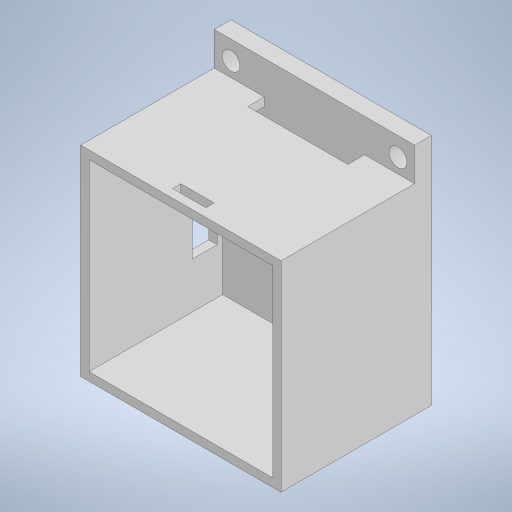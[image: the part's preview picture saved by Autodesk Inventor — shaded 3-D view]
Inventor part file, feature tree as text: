
AUTODESK INVENTOR PART (.ipt)
format: ipt  version: 2023 (Build 270158000, 158)  size: 266,240 bytes
history: native  units: in
note: dims shown in document units (in); Inventor stores cm internally (conversion verified against a paired STEP export)
features: extrude x5, sketch x5, projected_geometry x4
ambient origin geometry x8: Origin, YZ Plane, XZ Plane, XY Plane, X Axis, Y Axis, Z Axis, Center Point
bodies: Solid1 (feature_tree)
feature tree (14):
  extrude  "Extrusion1"  Depth=3.0in
  extrude  "Extrusion2"  Depth=1.5in
  extrude  "Extrusion4"  Depth=0.125in
  extrude  "Extrusion5"  Depth=0.125in
  extrude  "Extrusion6"  Depth=2.0in TaperAngle=0.0deg
  sketch  "Sketch1"  dims[d0=3.0in d1=3.0in]
  sketch  "Sketch2"  dims[d2=1.5in d3=1.5in]
  sketch  "Sketch4"  dims[d4=0.25in d5=0.0in d6=0.125in]
  projected_geometry  "Projected Loop1"
  sketch  "Sketch5"  dims[d7=0.125in d8=0.125in]
  projected_geometry  "Projected Loop2"
  sketch  "Sketch6"  dims[d9=0.125in d10=2.0in d11=0.0in d14=0.5625in d15=0.375in d16=0.25in d17=0.0in d18=0.27in d19=0.27in d20=2.5in d21=0.5in d22=0.2812in d23=0.2812in d24=0.25in d25=0.0in d26=1.5in d27=3.0in d28=1.5in d29=0.25in d30=0.5625in d31=0.0in d32=0.5in d33=0.125in d34=0.25in d35=0.125in]
  projected_geometry  "Projected Loop3"
  projected_geometry  "Projected Loop4"
